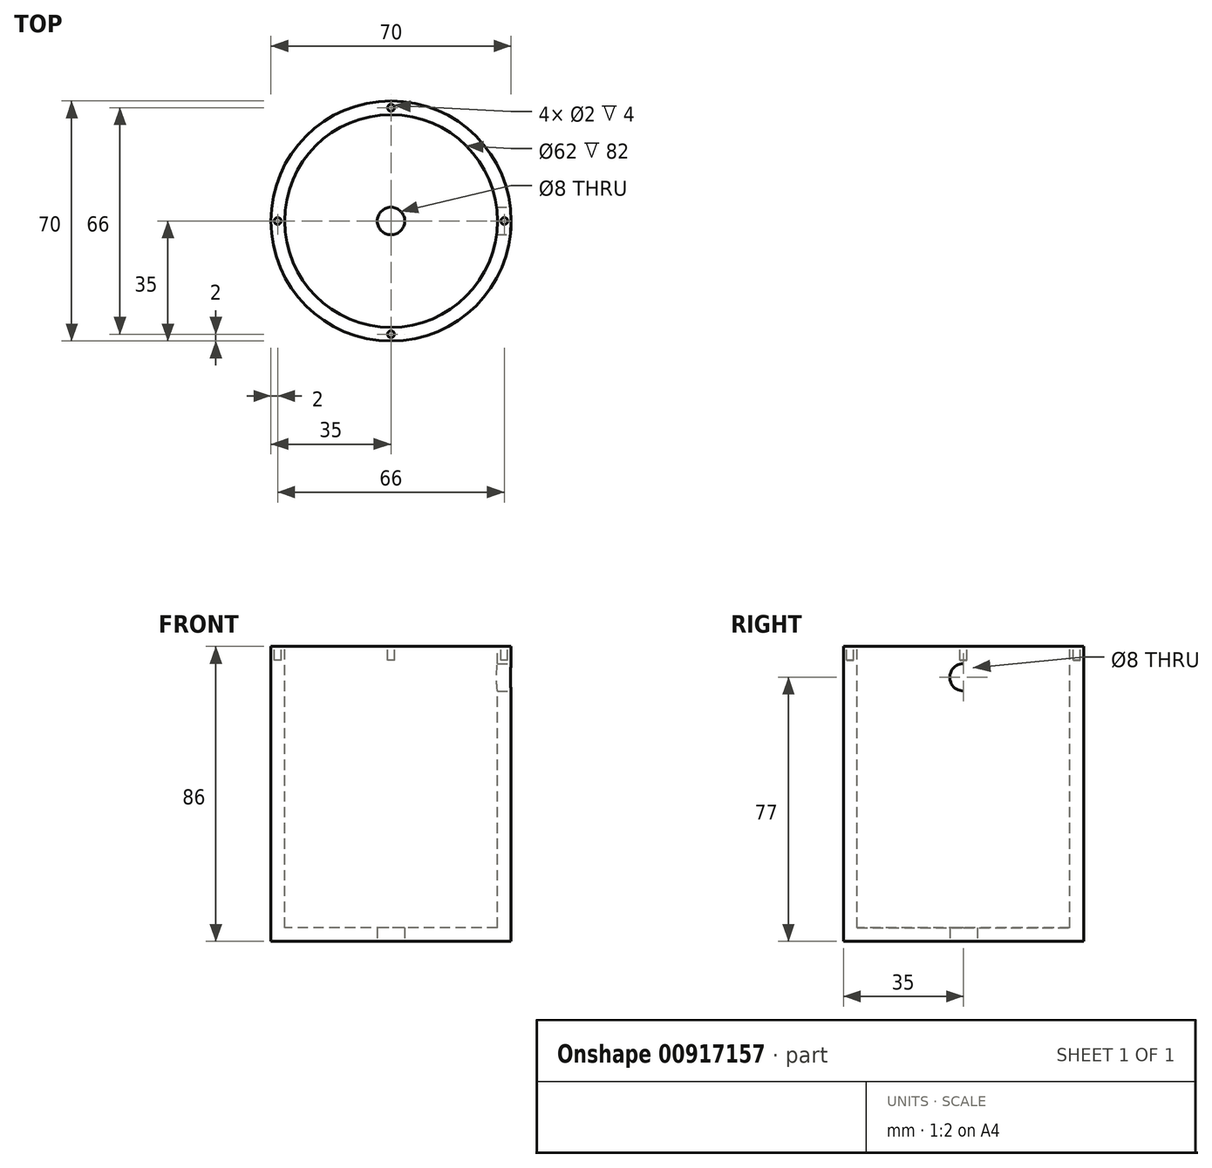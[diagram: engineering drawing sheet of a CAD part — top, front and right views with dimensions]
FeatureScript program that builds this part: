
annotation { "Feature Type Name" : "Feature", "Feature Type Description" : "" }
export const myFeature = defineFeature(function(context is Context, id is Id, definition is map)
    precondition{}
    {
        {
            var Q0;
            Q0=qCreatedBy(makeId("Top.planeOp"),FACE);
            var sketch = newSketch(context, id + "F0", { "sketchPlane" : qUnion([Q0])});
            skCircle(sketch, "E0", {"center": v(0, 0) * mm, "radius": 35 * mm});
            skSolve(sketch);
        }
        {
            var Q0;
            Q0 = qSketchRegion(id + "F0", true);
            extrude(context, id + "F1", {"entities" : qUnion([Q0]), "depth" : 86 * mm, "offsetDistance" : 25 * mm});
        }
        {
            var Q0;
            Q0=makeQuery(id+"F1.opExtrude","CAP_FACE",FACE,{"disambiguationData":[OSD([sQuery(id+"F0.wireOp",EDGE,"E0")])],"isStart":false});
            var sketch = newSketch(context, id + "F2", { "sketchPlane" : qUnion([Q0])});
            skCircle(sketch, "E1", {"center": v(0, 0) * mm, "radius": 31 * mm});
            skSolve(sketch);
        }
        {
            var Q0;
            Q0 = qSketchRegion(id + "F2", true);
            extrude(context, id + "F3", {"entities" : qUnion([Q0]), "operationType" : NewBodyOperationType.REMOVE, "oppositeDirection" : true, "depth" : 82 * mm, "offsetDistance" : 25 * mm});
        }
        {
            var Q0;
            Q0=makeQuery(id+"F1.opExtrude","CAP_FACE",FACE,{"disambiguationData":[OSD([sQuery(id+"F0.wireOp",EDGE,"E0")])],"isStart":true});
            var sketch = newSketch(context, id + "F4", { "sketchPlane" : qUnion([Q0])});
            skCircle(sketch, "E2", {"center": v(0, 0) * mm, "radius": 4 * mm});
            skSolve(sketch);
        }
        {
            var Q0;
            Q0 = qSketchRegion(id + "F4", true);
            extrude(context, id + "F5", {"entities" : qUnion([Q0]), "operationType" : NewBodyOperationType.REMOVE, "endBound" : BoundingType.UP_TO_NEXT, "oppositeDirection" : true, "depth" : 25 * mm, "offsetDistance" : 25 * mm});
        }
        {
            var Q0;
            Q0=makeQuery(id+"F1.opExtrude","CAP_FACE",FACE,{"disambiguationData":[OSD([sQuery(id+"F0.wireOp",EDGE,"E0")])],"isStart":false});
            var sketch = newSketch(context, id + "F6", { "sketchPlane" : qUnion([Q0])});
            skCircle(sketch, "E3", {"center": v(0, 33) * mm, "radius": 1 * mm});
            skCircle(sketch, "E4.1.0", {"center": v(-33, 0) * mm, "radius": 1 * mm});
            skCircle(sketch, "E4.2.0", {"center": v(0, -33) * mm, "radius": 1 * mm});
            skCircle(sketch, "E4.3.0", {"center": v(33, 0) * mm, "radius": 1 * mm});
            skPoint(sketch, "E4.center", {"position": v(0, 0) * mm});
            skSolve(sketch);
        }
        {
            var Q0;
            Q0 = qSketchRegion(id + "F6", true);
            extrude(context, id + "F7", {"entities" : qUnion([Q0]), "operationType" : NewBodyOperationType.REMOVE, "oppositeDirection" : true, "depth" : 4 * mm, "offsetDistance" : 25 * mm});
        }
        {
            var Q0;
            Q0=qCreatedBy(makeId("Right.planeOp"),FACE);
            cPlane(context, id + "F8", {"entities" : qUnion([Q0]), "cplaneType" : CPlaneType.OFFSET, "offset" : 35 * mm, "width" : 150 * mm, "height" : 150 * mm});
        }
        {
            var Q0;
            Q0=qCreatedBy(id+"F8.planeOp",FACE);
            var sketch = newSketch(context, id + "F9", { "sketchPlane" : qUnion([Q0])});
            skCircle(sketch, "E5", {"center": v(0, 77) * mm, "radius": 4 * mm});
            skSolve(sketch);
        }
        {
            var Q0;
            Q0=makeQuery(id+"F9.imprint","IMPRINT",FACE,{"disambiguationData":[TD([[makeQuery(id+"F9.imprint","IMPRINT",EDGE,{"derivedFrom":sQuery(id+"F9.wireOp",EDGE,"E5")}),1.0]])]});
            extrude(context, id + "F10", {"entities" : qUnion([Q0]), "operationType" : NewBodyOperationType.REMOVE, "endBound" : BoundingType.UP_TO_NEXT, "oppositeDirection" : true, "depth" : 25 * mm, "offsetDistance" : 25 * mm});
        }
    });
